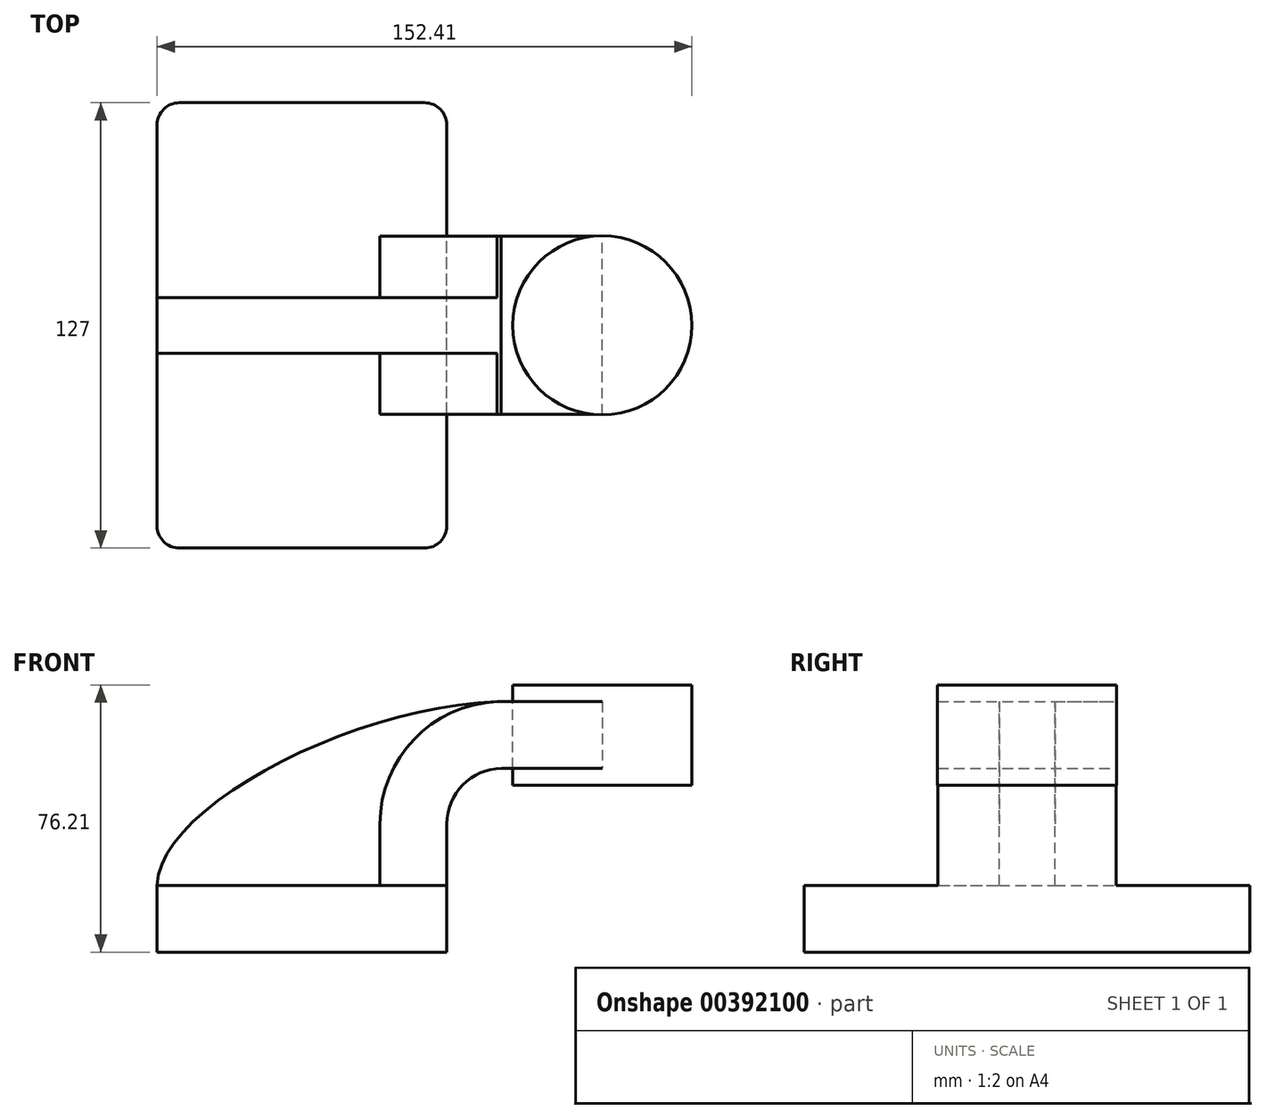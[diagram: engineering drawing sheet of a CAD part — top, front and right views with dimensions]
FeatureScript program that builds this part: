
annotation { "Feature Type Name" : "Feature", "Feature Type Description" : "" }
export const myFeature = defineFeature(function(context is Context, id is Id, definition is map)
    precondition{}
    {
        {
            var Q0;
            Q0=qCreatedBy(makeId("Front.planeOp"),FACE);
            var sketch = newSketch(context, id + "F0", { "sketchPlane" : qUnion([Q0])});
            skLineSegment(sketch, "E0.bottom", {"start": v(41.28, -9.52) * mm, "end": v(-41.28, -9.53) * mm});
            skLineSegment(sketch, "E0.top", {"start": v(41.28, 9.53) * mm, "end": v(-41.28, 9.53) * mm});
            skLineSegment(sketch, "E0.left", {"start": v(41.28, -9.52) * mm, "end": v(41.28, 9.53) * mm});
            skLineSegment(sketch, "E0.right", {"start": v(-41.28, -9.53) * mm, "end": v(-41.28, 9.53) * mm});
            skPoint(sketch, "E0.middle", {"position": v(0, 0) * mm});
            skLineSegment(sketch, "E1.bottom", {"start": v(60.32, 38.1) * mm, "end": v(111.12, 38.1) * mm});
            skLineSegment(sketch, "E1.top", {"start": v(60.32, 66.68) * mm, "end": v(111.12, 66.68) * mm});
            skLineSegment(sketch, "E1.left", {"start": v(60.32, 38.1) * mm, "end": v(60.32, 66.68) * mm});
            skLineSegment(sketch, "E1.right", {"start": v(111.12, 38.1) * mm, "end": v(111.12, 66.68) * mm});
            skPoint(sketch, "E1.middle", {"position": v(85.72, 52.39) * mm});
            skLineSegment(sketch, "E2", {"start": v(41.28, 9.53) * mm, "end": v(41.28, 27) * mm});
            skArc(sketch, "E3", {"start": v(41.28, 27) * mm, "mid": v(45.83, 38.14) * mm, "end": v(56.9, 42.88) * mm});
            skLineSegment(sketch, "E4", {"start": v(56.9, 42.88) * mm, "end": v(85.6, 42.88) * mm});
            skLineSegment(sketch, "E5.0", {"start": v(56.77, 61.93) * mm, "end": v(85.6, 61.93) * mm});
            skArc(sketch, "E5.1", {"start": v(22.23, 27) * mm, "mid": v(32.32, 51.56) * mm, "end": v(56.77, 61.93) * mm});
            skLineSegment(sketch, "E5.2", {"start": v(22.22, 9.53) * mm, "end": v(22.22, 27) * mm});
            skLineSegment(sketch, "E6", {"start": v(85.6, 61.93) * mm, "end": v(85.6, 42.88) * mm});
            skFitSpline(sketch, "E7", {"points": [v(-41.28, 9.52) * mm, v(56.77, 61.93) * mm], "startDerivative": vector(1.3, 67.62) * mm, "endDerivative": vector(124.4, 2.6) * mm});
            skFitSpline(sketch, "E8", {"points": [v(32.1, 58.85) * mm, v(32.1, 59.88) * mm], "startDerivative": vector(0, 1.02) * mm, "endDerivative": vector(0, 1.02) * mm});
            skLineSegment(sketch, "E9", {"start": v(85.6, 66.68) * mm, "end": v(85.6, 38.1) * mm});
            skSolve(sketch);
        }
        {
            var Q0;
            Q0=makeQuery(id+"F0.imprint","IMPRINT",FACE,{"disambiguationData":[TD([[makeQuery(id+"F0.imprint","IMPRINT",EDGE,{"derivedFrom":sQuery(id+"F0.wireOp",EDGE,"E0.bottom")}),-1.0]])]});
            extrude(context, id + "F1", {"entities" : qUnion([Q0]), "endBound" : BoundingType.SYMMETRIC, "depth" : 127 * mm});
        }
        {
            var Q0;
            {var subQ1=sQuery(id+"F0.wireOp",EDGE,"E2");Q0=makeQuery(id+"F0.imprint","IMPRINT",FACE,{"disambiguationData":[TD([[makeQuery(id+"F0.imprint","IMPRINT",EDGE,{"derivedFrom":subQ1}),1.0]])]});}
            var Q1;
            {var subQ0=sQuery(id+"F0.wireOp",EDGE,"E4");var subQ1=sQuery(id+"F0.wireOp",EDGE,"E1.left");var subQ2=makeQuery(id+"F0.imprint","INTERSECT",VERTEX,{"derivedFrom":[subQ1,subQ0]});Q1=makeQuery(id+"F0.imprint","IMPRINT",FACE,{"disambiguationData":[TD([[makeQuery(id+"F0.imprint","IMPRINT",EDGE,{"disambiguationData":[TD([[subQ2,-1.0]])],"derivedFrom":subQ1}),-1.0]])]});}
            extrude(context, id + "F2", {"entities" : qUnion([Q0, Q1]), "operationType" : NewBodyOperationType.ADD, "endBound" : BoundingType.SYMMETRIC, "depth" : 50.8 * mm});
        }
        {
            var Q0;
            {var subQ3=sQuery(id+"F0.wireOp",EDGE,"E5.2");Q0=makeQuery(id+"F0.imprint","IMPRINT",FACE,{"disambiguationData":[TD([[makeQuery(id+"F0.imprint","IMPRINT",EDGE,{"derivedFrom":subQ3}),1.0]])]});}
            extrude(context, id + "F3", {"entities" : qUnion([Q0]), "operationType" : NewBodyOperationType.ADD, "endBound" : BoundingType.SYMMETRIC, "depth" : 15.88 * mm});
        }
        {
            var Q0;
            {var subQ4=sQuery(id+"F0.wireOp",EDGE,"E1.right");Q0=makeQuery(id+"F0.imprint","IMPRINT",FACE,{"disambiguationData":[TD([[makeQuery(id+"F0.imprint","IMPRINT",EDGE,{"derivedFrom":subQ4}),1.0]])]});}
            var Q1;
            Q1=sQuery(id+"F0.wireOp",EDGE,"E9");
            revolve(context, id + "F4", {"entities" : qUnion([Q0]), "axis" : qUnion([Q1]), "revolveType" : RevolveType.FULL});
        }
        {
            var Q0;
            Q0=makeQuery(id+"F1.opExtrude","CAP_EDGE",EDGE,{"disambiguationData":[OSD([sQuery(id+"F0.wireOp",EDGE,"E0.left")])],"isStart":false});
            var Q1;
            Q1=makeQuery(id+"F1.opExtrude","CAP_EDGE",EDGE,{"disambiguationData":[OSD([sQuery(id+"F0.wireOp",EDGE,"E0.right")])],"isStart":false});
            var Q2;
            Q2=makeQuery(id+"F1.opExtrude","CAP_EDGE",EDGE,{"disambiguationData":[OSD([sQuery(id+"F0.wireOp",EDGE,"E0.left")])],"isStart":true});
            var Q3;
            Q3=makeQuery(id+"F1.opExtrude","CAP_EDGE",EDGE,{"disambiguationData":[OSD([sQuery(id+"F0.wireOp",EDGE,"E0.right")])],"isStart":true});
            fillet(context, id + "F5", {"entities" : qUnion([Q0, Q1, Q2, Q3]), "radius" : 6.35 * mm, "tangentPropagation" : true, "allowEdgeOverflow" : false});
        }
    });
